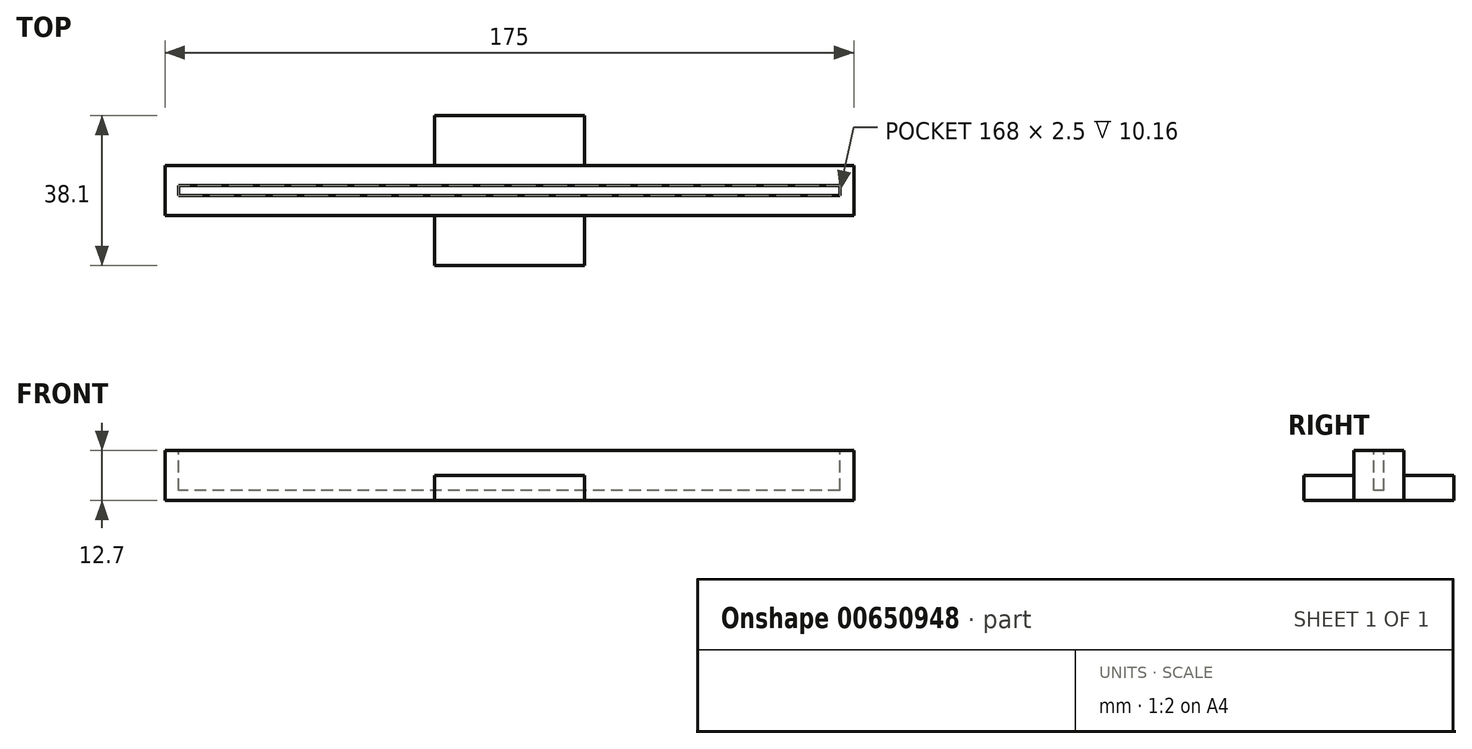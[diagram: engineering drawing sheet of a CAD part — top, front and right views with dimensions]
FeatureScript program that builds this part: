
annotation { "Feature Type Name" : "Feature", "Feature Type Description" : "" }
export const myFeature = defineFeature(function(context is Context, id is Id, definition is map)
    precondition{}
    {
        {
            var Q0;
            Q0=qCreatedBy(makeId("Top.planeOp"),FACE);
            var sketch = newSketch(context, id + "F0", { "sketchPlane" : qUnion([Q0])});
            skLineSegment(sketch, "E0.bottom", {"start": v(87.5, 6.35) * mm, "end": v(-87.5, 6.35) * mm});
            skLineSegment(sketch, "E0.top", {"start": v(87.5, -6.35) * mm, "end": v(-87.5, -6.35) * mm});
            skLineSegment(sketch, "E0.left", {"start": v(87.5, 6.35) * mm, "end": v(87.5, -6.35) * mm});
            skLineSegment(sketch, "E0.right", {"start": v(-87.5, 6.35) * mm, "end": v(-87.5, -6.35) * mm});
            skPoint(sketch, "E0.middle", {"position": v(0, 0) * mm});
            skSolve(sketch);
        }
        {
            var Q0;
            Q0=makeQuery(id+"F0.imprint","IMPRINT",FACE,{"disambiguationData":[TD([[makeQuery(id+"F0.imprint","IMPRINT",EDGE,{"derivedFrom":sQuery(id+"F0.wireOp",EDGE,"E0.bottom")}),1.0]])]});
            extrude(context, id + "F1", {"entities" : qUnion([Q0]), "depth" : 12.7 * mm, "offsetDistance" : 25.4 * mm});
        }
        {
            var Q0;
            Q0=makeQuery(id+"F1.opExtrude","CAP_FACE",FACE,{"disambiguationData":[OSD([sQuery(id+"F0.wireOp",EDGE,"E0.bottom"),sQuery(id+"F0.wireOp",EDGE,"E0.top"),sQuery(id+"F0.wireOp",EDGE,"E0.left"),sQuery(id+"F0.wireOp",EDGE,"E0.right")])],"isStart":true});
            var sketch = newSketch(context, id + "F2", { "sketchPlane" : qUnion([Q0])});
            skLineSegment(sketch, "E1.bottom", {"start": v(19.05, 19.05) * mm, "end": v(-19.05, 19.05) * mm});
            skLineSegment(sketch, "E1.top", {"start": v(19.05, -19.05) * mm, "end": v(-19.05, -19.05) * mm});
            skLineSegment(sketch, "E1.left", {"start": v(19.05, 19.05) * mm, "end": v(19.05, -19.05) * mm});
            skLineSegment(sketch, "E1.right", {"start": v(-19.05, 19.05) * mm, "end": v(-19.05, -19.05) * mm});
            skPoint(sketch, "E1.middle", {"position": v(0, 0) * mm});
            skSolve(sketch);
        }
        {
            var Q0;
            {var subQ0=sQuery(id+"F2.wireOp",EDGE,"E1.top");Q0=makeQuery(id+"F2.imprint","IMPRINT",FACE,{"disambiguationData":[TD([[makeQuery(id+"F2.imprint","IMPRINT",EDGE,{"derivedFrom":subQ0}),-1.0]])]});}
            var Q1;
            {var subQ0=sQuery(id+"F2.wireOp",EDGE,"E1.left");var subQ1=makeQuery(id+"F1.opExtrude","CAP_EDGE",EDGE,{"disambiguationData":[OSD([sQuery(id+"F0.wireOp",EDGE,"E0.top")])],"isStart":true});var subQ2=makeQuery(id+"F2.imprint","INTERSECT",VERTEX,{"derivedFrom":[subQ1,subQ0]});Q1=makeQuery(id+"F2.imprint","IMPRINT",FACE,{"disambiguationData":[TD([[makeQuery(id+"F2.imprint","IMPRINT",EDGE,{"disambiguationData":[TD([[subQ2,-1.0]])],"derivedFrom":subQ0}),-1.0]])]});}
            var Q2;
            {var subQ0=sQuery(id+"F2.wireOp",EDGE,"E1.bottom");Q2=makeQuery(id+"F2.imprint","IMPRINT",FACE,{"disambiguationData":[TD([[makeQuery(id+"F2.imprint","IMPRINT",EDGE,{"derivedFrom":subQ0}),1.0]])]});}
            extrude(context, id + "F3", {"entities" : qUnion([Q0, Q1, Q2]), "operationType" : NewBodyOperationType.ADD, "oppositeDirection" : true, "depth" : 6.35 * mm, "offsetDistance" : 25.4 * mm});
        }
        {
            var Q0;
            Q0=makeQuery(id+"F1.opExtrude","CAP_FACE",FACE,{"disambiguationData":[OSD([sQuery(id+"F0.wireOp",EDGE,"E0.bottom"),sQuery(id+"F0.wireOp",EDGE,"E0.top"),sQuery(id+"F0.wireOp",EDGE,"E0.left"),sQuery(id+"F0.wireOp",EDGE,"E0.right")])],"isStart":false});
            var sketch = newSketch(context, id + "F4", { "sketchPlane" : qUnion([Q0])});
            skLineSegment(sketch, "E2.bottom", {"start": v(84, 1.25) * mm, "end": v(-84, 1.25) * mm});
            skLineSegment(sketch, "E2.top", {"start": v(84, -1.25) * mm, "end": v(-84, -1.25) * mm});
            skLineSegment(sketch, "E2.left", {"start": v(84, 1.25) * mm, "end": v(84, -1.25) * mm});
            skLineSegment(sketch, "E2.right", {"start": v(-84, 1.25) * mm, "end": v(-84, -1.25) * mm});
            skPoint(sketch, "E2.middle", {"position": v(0, 0) * mm});
            skSolve(sketch);
        }
        {
            var Q0;
            Q0=makeQuery(id+"F4.imprint","IMPRINT",FACE,{"disambiguationData":[TD([[makeQuery(id+"F4.imprint","IMPRINT",EDGE,{"derivedFrom":sQuery(id+"F4.wireOp",EDGE,"E2.bottom")}),1.0]])]});
            extrude(context, id + "F5", {"entities" : qUnion([Q0]), "operationType" : NewBodyOperationType.REMOVE, "oppositeDirection" : true, "depth" : 10.16 * mm, "offsetDistance" : 25.4 * mm});
        }
    });
